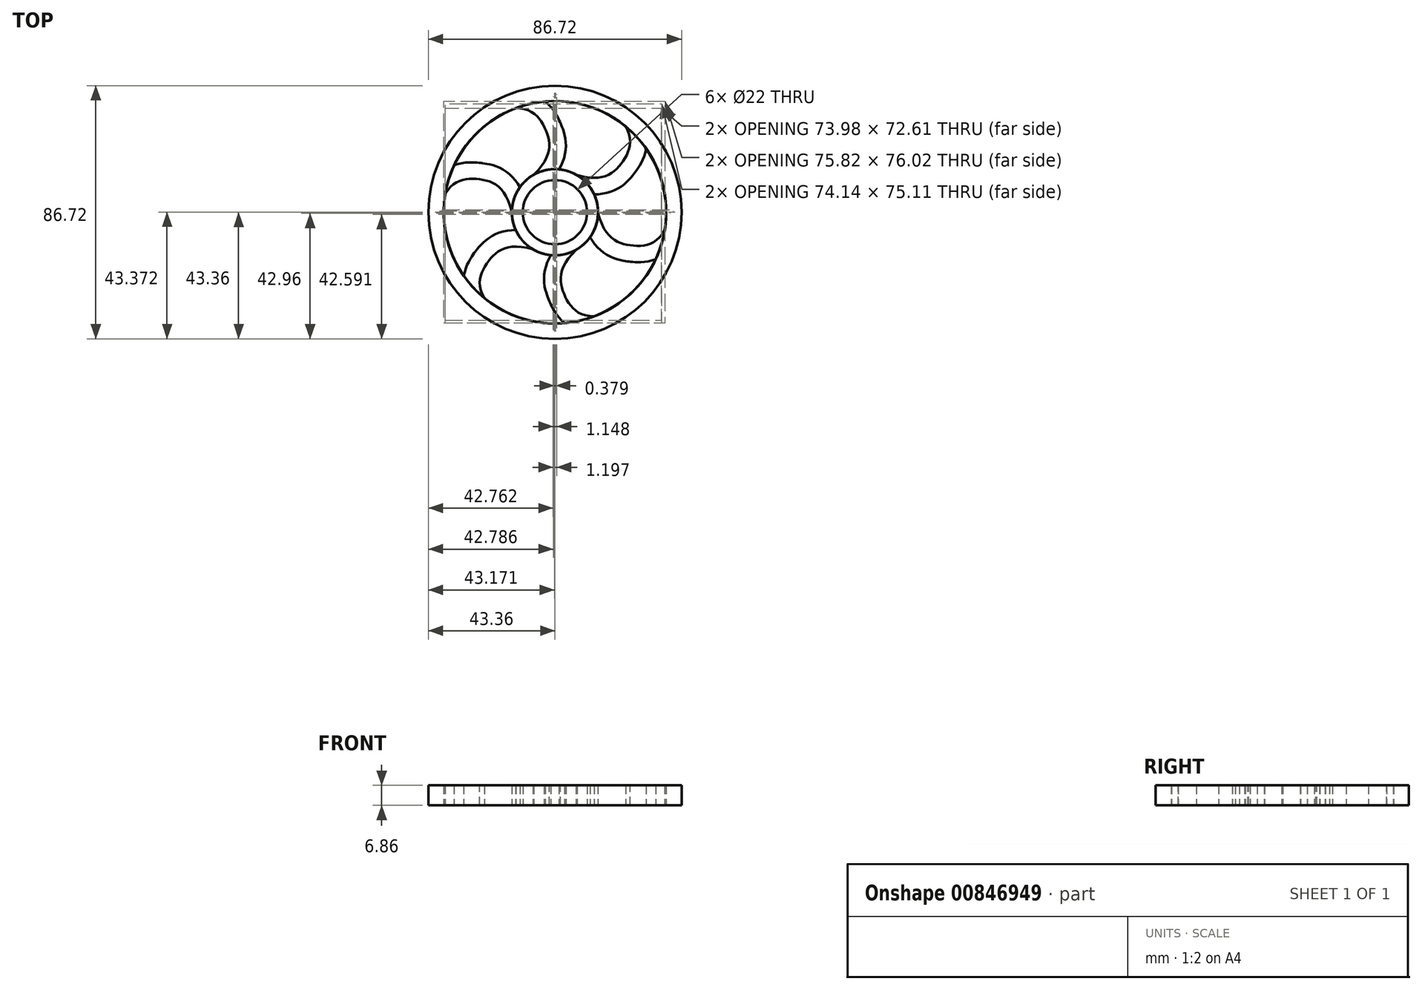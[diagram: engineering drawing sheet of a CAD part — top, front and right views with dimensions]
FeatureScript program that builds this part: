
annotation { "Feature Type Name" : "Feature", "Feature Type Description" : "" }
export const myFeature = defineFeature(function(context is Context, id is Id, definition is map)
    precondition{}
    {
        {
            var Q0;
            Q0=qCreatedBy(makeId("Top.planeOp"),FACE);
            var sketch = newSketch(context, id + "F0", { "sketchPlane" : qUnion([Q0])});
            skCircle(sketch, "E0", {"center": v(0, 0) * mm, "radius": 11 * mm});
            skCircle(sketch, "E1", {"center": v(0, 0) * mm, "radius": 14.76 * mm});
            skFitSpline(sketch, "E2", {"points": [v(-7.22, 12.87) * mm, v(-3.14, 28.1) * mm, v(-13.4, 35.67) * mm], "startDerivative": vector(36.84, 36.34) * mm, "endDerivative": vector(-37.99, -0.26) * mm});
            skFitSpline(sketch, "E3.0", {"points": [v(-3.3, 8.9) * mm, v(-2.4, 9.78) * mm, v(-0.8, 11.53) * mm, v(1.1, 14.18) * mm, v(2.52, 16.9) * mm, v(3.4, 19.69) * mm, v(3.73, 22.46) * mm, v(3.58, 25.06) * mm, v(3.15, 27.02) * mm, v(2.71, 28.45) * mm, v(2.4, 29.29) * mm, v(2.15, 29.93) * mm, v(1.96, 30.4) * mm, v(1.75, 30.86) * mm, v(1.46, 31.5) * mm, v(1.07, 32.3) * mm, v(0.35, 33.62) * mm, v(-0.75, 35.28) * mm, v(-2.45, 37.2) * mm, v(-4.62, 38.93) * mm, v(-7.23, 40.28) * mm, v(-10.2, 41.1) * mm, v(-12.34, 41.26) * mm, v(-13.44, 41.25) * mm]});
            skCircle(sketch, "E4", {"center": v(0, 0) * mm, "radius": 38.1 * mm});
            skCircle(sketch, "E5", {"center": v(0, 0) * mm, "radius": 43.36 * mm});
            skSolve(sketch);
        }
        {
            var Q0;
            {var subQ0=sQuery(id+"F0.wireOp",EDGE,"E2");Q0=makeQuery(id+"F0.imprint","IMPRINT",FACE,{"disambiguationData":[TD([[makeQuery(id+"F0.imprint","IMPRINT",EDGE,{"derivedFrom":subQ0}),-1.0]])]});}
            var Q1;
            Q1=makeQuery(id+"F0.imprint","IMPRINT",FACE,{"disambiguationData":[TD([[makeQuery(id+"F0.imprint","IMPRINT",EDGE,{"derivedFrom":sQuery(id+"F0.wireOp",EDGE,"E0")}),-1.0]])]});
            var Q2;
            Q2=makeQuery(id+"F0.imprint","IMPRINT",FACE,{"disambiguationData":[TD([[makeQuery(id+"F0.imprint","IMPRINT",EDGE,{"derivedFrom":sQuery(id+"F0.wireOp",EDGE,"E5")}),1.0]])]});
            extrude(context, id + "F1", {"entities" : qUnion([Q0, Q1, Q2]), "depth" : 6.86 * mm, "offsetDistance" : 25.4 * mm});
        }
        {
            var Q0;
            Q0=makeQuery(id+"F1.opExtrude","SWEPT_BODY",BODY,{"disambiguationData":[OSD([sQuery(id+"F0.wireOp",EDGE,"E0"),sQuery(id+"F0.wireOp",EDGE,"E1"),sQuery(id+"F0.wireOp",EDGE,"E2"),sQuery(id+"F0.wireOp",EDGE,"E3.0"),sQuery(id+"F0.wireOp",EDGE,"E4"),sQuery(id+"F0.wireOp",EDGE,"E5")])]});
            var Q1;
            Q1=makeQuery(id+"F1.opExtrude","CAP_EDGE",EDGE,{"disambiguationData":[OSD([sQuery(id+"F0.wireOp",EDGE,"E0")])],"isStart":false});
            circularPattern(context, id + "F2", {"entities" : qUnion([Q0]), "axis" : qUnion([Q1]), "angle" : 360 * degree, "instanceCount" : 6, "equalSpace" : true});
        }
    });
